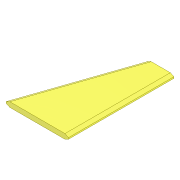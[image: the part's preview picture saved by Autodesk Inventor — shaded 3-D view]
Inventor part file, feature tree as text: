
AUTODESK INVENTOR PART (.ipt)
format: ipt  version: 2022 (Build 260153000, 153)  size: 104,448 bytes
history: native  units: mm
features: chamfer x4, extrude x2, sketch x2, plane x1, projected_geometry x1
ambient origin geometry x8: Origin, YZ Plane, XZ Plane, XY Plane, X Axis, Y Axis, Z Axis, Center Point
bodies: Solid1 (feature_tree)
feature tree (10):
  extrude  "Extrusion1"  Depth=355.0mm
  extrude  "Extrusion2"  Depth=28.0mm TaperAngle=0.0deg
  plane  "Work Plane1"
  chamfer  "Chamfer1"  Distance=150.0mm
  chamfer  "Chamfer2"  [1 undecoded]
  chamfer  "Chamfer3"  Distance=20.0mm Angle=45.0deg
  chamfer  "Chamfer4"  Distance=10.0mm Angle=45.0deg
  sketch  "Sketch1"  dims[d0=600.0mm d1=355.0mm]
  sketch  "Sketch2"  dims[d2=28.0mm d3=0.0mm d5=200.0mm d6=0.0mm d7=150.0mm d8=0.0mm d23=20.0mm d24=10.0mm d25=45.0deg d26=10.0mm d27=20.0mm d28=45.0deg d29=20.0mm d30=10.0mm d31=45.0deg d32=20.0mm d33=10.0mm d34=45.0deg]
  projected_geometry  "Projected Loop1"
note: 1 required parameter value undecoded (feature->parameter linkage not recoverable at this tier; creation-order binding heuristic only, values carry confidence <= 0.55)
